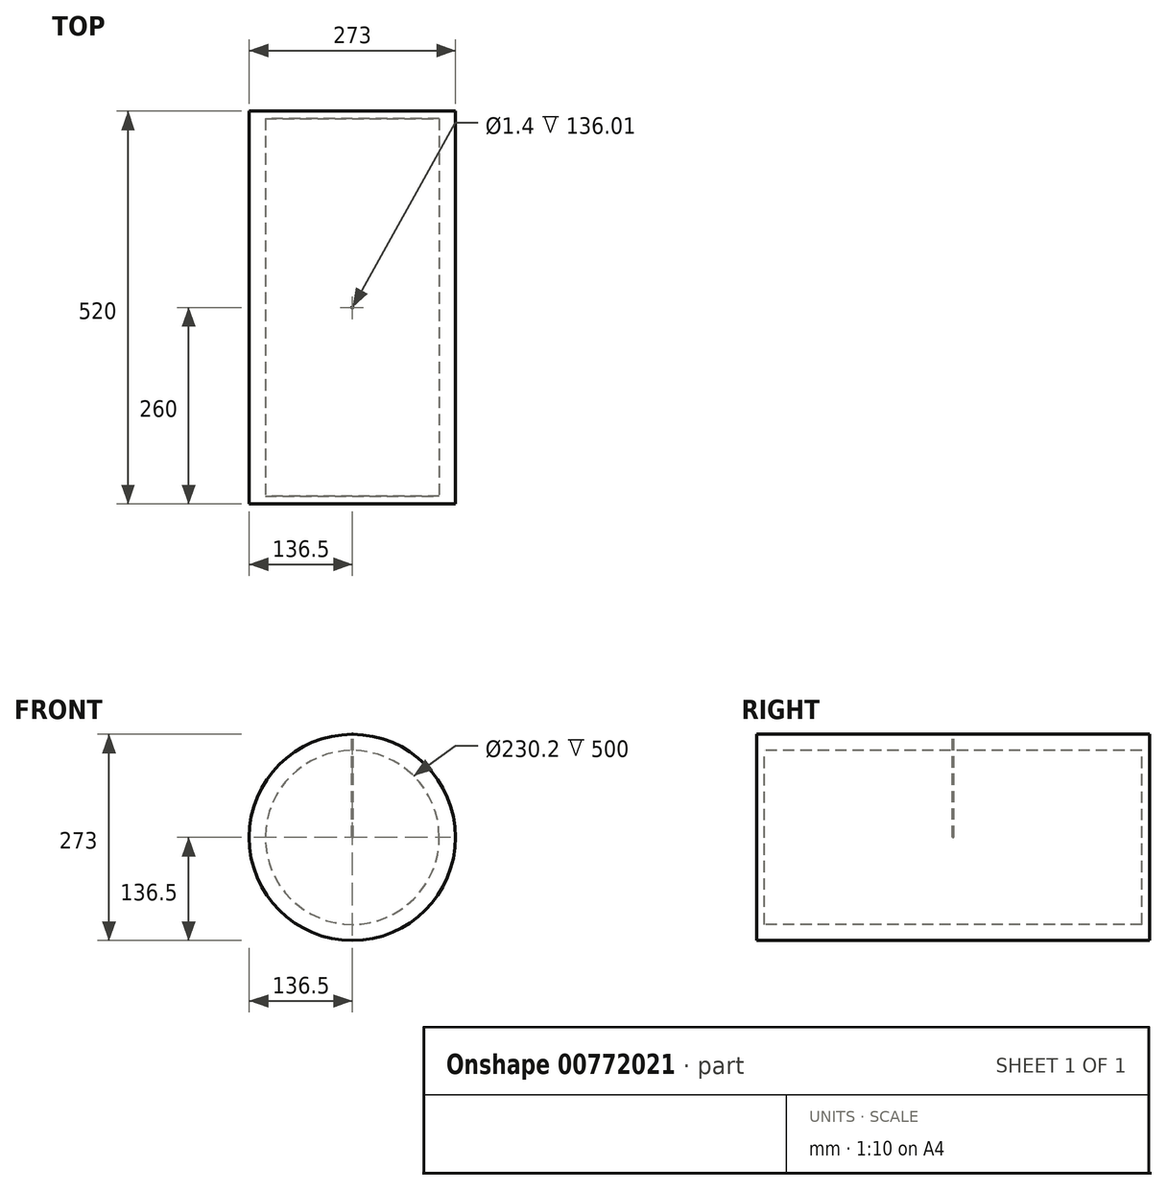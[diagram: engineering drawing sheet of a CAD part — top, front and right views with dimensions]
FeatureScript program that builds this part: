
annotation { "Feature Type Name" : "Feature", "Feature Type Description" : "" }
export const myFeature = defineFeature(function(context is Context, id is Id, definition is map)
    precondition{}
    {
        {
            var Q0;
            Q0=qCreatedBy(makeId("Right.planeOp"),FACE);
            var sketch = newSketch(context, id + "F0", { "sketchPlane" : qUnion([Q0])});
            skLineSegment(sketch, "E0", {"start": v(0, 0) * mm, "end": v(1, 0) * mm});
            skLineSegment(sketch, "E1", {"start": v(0, 0) * mm, "end": v(-1, 0) * mm});
            skLineSegment(sketch, "E2", {"start": v(-1, 0) * mm, "end": v(-1, -136) * mm});
            skLineSegment(sketch, "E3", {"start": v(1, 0) * mm, "end": v(1, -136.01) * mm});
            skArc(sketch, "E4", {"start": v(1, -136) * mm, "mid": v(0, -137) * mm, "end": v(-1, -136) * mm});
            skPoint(sketch, "E5", {"position": v(-0.7, 0) * mm});
            skPoint(sketch, "E6", {"position": v(0.7, 0) * mm});
            skLineSegment(sketch, "E7", {"start": v(-0.7, 0) * mm, "end": v(-0.7, -136) * mm});
            skLineSegment(sketch, "E8", {"start": v(0.7, 0) * mm, "end": v(0.7, -136) * mm});
            skLineSegment(sketch, "E9", {"start": v(-0.7, -136) * mm, "end": v(0.7, -136) * mm});
            skLineSegment(sketch, "E10", {"start": v(0, 763.5) * mm, "end": v(0, -236.5) * mm});
            skPoint(sketch, "E11", {"position": v(0, -21.4) * mm});
            skLineSegment(sketch, "E12", {"start": v(0, -21.4) * mm, "end": v(-250, -21.4) * mm});
            skLineSegment(sketch, "E13", {"start": v(0, 0) * mm, "end": v(-250, 0) * mm});
            skLineSegment(sketch, "E14", {"start": v(0, -21.4) * mm, "end": v(250, -21.4) * mm});
            skLineSegment(sketch, "E15", {"start": v(0, 0) * mm, "end": v(250, 0) * mm});
            skLineSegment(sketch, "E16", {"start": v(250, 0) * mm, "end": v(250, -21.4) * mm});
            skLineSegment(sketch, "E17", {"start": v(-250, 0) * mm, "end": v(-250, -21.4) * mm});
            skLineSegment(sketch, "E18", {"start": v(-250, 0) * mm, "end": v(-260, 0) * mm});
            skLineSegment(sketch, "E19", {"start": v(-260, 0) * mm, "end": v(-260, -21.4) * mm});
            skLineSegment(sketch, "E20", {"start": v(-260, -21.4) * mm, "end": v(-250, -21.4) * mm});
            skLineSegment(sketch, "E21", {"start": v(250, 0) * mm, "end": v(260, 0) * mm});
            skLineSegment(sketch, "E22", {"start": v(260, 0) * mm, "end": v(260, -21.4) * mm});
            skLineSegment(sketch, "E23", {"start": v(260, -21.4) * mm, "end": v(250, -21.4) * mm});
            skLineSegment(sketch, "E24", {"start": v(-260, -136.5) * mm, "end": v(260, -136.5) * mm});
            skLineSegment(sketch, "E25", {"start": v(-250, -21.4) * mm, "end": v(-250, -136.5) * mm});
            skLineSegment(sketch, "E26", {"start": v(-260, -21.4) * mm, "end": v(-260, -136.5) * mm});
            skLineSegment(sketch, "E27", {"start": v(260, -21.4) * mm, "end": v(260, -136.5) * mm});
            skLineSegment(sketch, "E28", {"start": v(250, -21.4) * mm, "end": v(250, -136.5) * mm});
            skSolve(sketch);
        }
        {
            var Q0;
            {var subQ5=sQuery(id+"F0.wireOp",EDGE,"E12");var subQ8=sQuery(id+"F0.wireOp",EDGE,"E2");var subQ13=makeQuery(id+"F0.imprint","INTERSECT",VERTEX,{"derivedFrom":[subQ8,subQ5]});Q0=makeQuery(id+"F0.imprint","IMPRINT",FACE,{"disambiguationData":[TD([[makeQuery(id+"F0.imprint","IMPRINT",EDGE,{"disambiguationData":[TD([[subQ13,-1.0]])],"derivedFrom":subQ8}),1.0]])]});}
            var Q1;
            {var subQ0=sQuery(id+"F0.wireOp",EDGE,"E10");var subQ1=sQuery(id+"F0.wireOp",EDGE,"E4");var subQ2=makeQuery(id+"F0.imprint","INTERSECT",VERTEX,{"derivedFrom":[subQ1,subQ0]});Q1=makeQuery(id+"F0.imprint","IMPRINT",FACE,{"disambiguationData":[TD([[makeQuery(id+"F0.imprint","IMPRINT",EDGE,{"disambiguationData":[TD([[subQ2,-1.0]])],"derivedFrom":subQ1}),-1.0]])]});}
            var Q2;
            {var subQ3=sQuery(id+"F0.wireOp",EDGE,"E7");var subQ5=sQuery(id+"F0.wireOp",EDGE,"E12");var subQ6=makeQuery(id+"F0.imprint","INTERSECT",VERTEX,{"derivedFrom":[subQ3,subQ5]});Q2=makeQuery(id+"F0.imprint","IMPRINT",FACE,{"disambiguationData":[TD([[makeQuery(id+"F0.imprint","IMPRINT",EDGE,{"disambiguationData":[TD([[subQ6,1.0]])],"derivedFrom":subQ3}),-1.0]])]});}
            var Q3;
            Q3=sQuery(id+"F0.wireOp",EDGE,"E10");
            revolve(context, id + "F1", {"surfaceOperationType" : NewSurfaceOperationType.NEW, "entities" : qUnion([Q0, Q1, Q2]), "axis" : qUnion([Q3]), "revolveType" : RevolveType.FULL});
        }
        {
            var Q0;
            {var subQ3=sQuery(id+"F0.wireOp",EDGE,"E7");var subQ5=sQuery(id+"F0.wireOp",EDGE,"E12");var subQ6=makeQuery(id+"F0.imprint","INTERSECT",VERTEX,{"derivedFrom":[subQ3,subQ5]});Q0=qUnion([makeQuery(id+"F0.imprint","IMPRINT",FACE,{"disambiguationData":[TD([[makeQuery(id+"F0.imprint","IMPRINT",EDGE,{"disambiguationData":[TD([[subQ6,-1.0]])],"derivedFrom":subQ3}),1.0]])]}),makeQuery(id+"F0.imprint","IMPRINT",FACE,{"disambiguationData":[TD([[makeQuery(id+"F0.imprint","IMPRINT",EDGE,{"disambiguationData":[TD([[subQ6,1.0]])],"derivedFrom":subQ3}),1.0]])]})]);}
            var Q1;
            Q1=sQuery(id+"F0.wireOp",EDGE,"E10");
            revolve(context, id + "F2", {"surfaceOperationType" : NewSurfaceOperationType.NEW, "entities" : qUnion([Q0]), "axis" : qUnion([Q1]), "revolveType" : RevolveType.FULL});
        }
        {
            var Q0;
            Q0=makeQuery(id+"F0.imprint","IMPRINT",FACE,{"disambiguationData":[TD([[makeQuery(id+"F0.imprint","IMPRINT",EDGE,{"derivedFrom":sQuery(id+"F0.wireOp",EDGE,"E16")}),1.0]])]});
            var Q1;
            Q1=makeQuery(id+"F0.imprint","IMPRINT",FACE,{"disambiguationData":[TD([[makeQuery(id+"F0.imprint","IMPRINT",EDGE,{"derivedFrom":sQuery(id+"F0.wireOp",EDGE,"E23")}),1.0]])]});
            var Q2;
            {var subQ0=sQuery(id+"F0.wireOp",EDGE,"E15");Q2=makeQuery(id+"F0.imprint","IMPRINT",FACE,{"disambiguationData":[TD([[makeQuery(id+"F0.imprint","IMPRINT",EDGE,{"derivedFrom":subQ0}),-1.0]])]});}
            var Q3;
            {var subQ0=sQuery(id+"F0.wireOp",EDGE,"E13");Q3=makeQuery(id+"F0.imprint","IMPRINT",FACE,{"disambiguationData":[TD([[makeQuery(id+"F0.imprint","IMPRINT",EDGE,{"derivedFrom":subQ0}),1.0]])]});}
            var Q4;
            {var subQ3=sQuery(id+"F0.wireOp",EDGE,"E8");var subQ5=sQuery(id+"F0.wireOp",EDGE,"E14");var subQ7=makeQuery(id+"F0.imprint","INTERSECT",VERTEX,{"derivedFrom":[subQ3,subQ5]});Q4=makeQuery(id+"F0.imprint","IMPRINT",FACE,{"disambiguationData":[TD([[makeQuery(id+"F0.imprint","IMPRINT",EDGE,{"disambiguationData":[TD([[subQ7,1.0]])],"derivedFrom":subQ3}),1.0]])]});}
            var Q5;
            {var subQ3=sQuery(id+"F0.wireOp",EDGE,"E7");var subQ5=sQuery(id+"F0.wireOp",EDGE,"E12");var subQ6=makeQuery(id+"F0.imprint","INTERSECT",VERTEX,{"derivedFrom":[subQ3,subQ5]});Q5=makeQuery(id+"F0.imprint","IMPRINT",FACE,{"disambiguationData":[TD([[makeQuery(id+"F0.imprint","IMPRINT",EDGE,{"disambiguationData":[TD([[subQ6,1.0]])],"derivedFrom":subQ3}),-1.0]])]});}
            var Q6;
            {var subQ3=sQuery(id+"F0.wireOp",EDGE,"E8");var subQ5=sQuery(id+"F0.wireOp",EDGE,"E14");var subQ6=makeQuery(id+"F0.imprint","INTERSECT",VERTEX,{"derivedFrom":[subQ3,subQ5]});Q6=makeQuery(id+"F0.imprint","IMPRINT",FACE,{"disambiguationData":[TD([[makeQuery(id+"F0.imprint","IMPRINT",EDGE,{"disambiguationData":[TD([[subQ6,1.0]])],"derivedFrom":subQ3}),-1.0]])]});}
            var Q7;
            {var subQ3=sQuery(id+"F0.wireOp",EDGE,"E7");var subQ5=sQuery(id+"F0.wireOp",EDGE,"E12");var subQ6=makeQuery(id+"F0.imprint","INTERSECT",VERTEX,{"derivedFrom":[subQ3,subQ5]});Q7=makeQuery(id+"F0.imprint","IMPRINT",FACE,{"disambiguationData":[TD([[makeQuery(id+"F0.imprint","IMPRINT",EDGE,{"disambiguationData":[TD([[subQ6,1.0]])],"derivedFrom":subQ3}),1.0]])]});}
            var Q8;
            Q8=makeQuery(id+"F0.imprint","IMPRINT",FACE,{"disambiguationData":[TD([[makeQuery(id+"F0.imprint","IMPRINT",EDGE,{"derivedFrom":sQuery(id+"F0.wireOp",EDGE,"E17")}),-1.0]])]});
            var Q9;
            Q9=makeQuery(id+"F0.imprint","IMPRINT",FACE,{"disambiguationData":[TD([[makeQuery(id+"F0.imprint","IMPRINT",EDGE,{"derivedFrom":sQuery(id+"F0.wireOp",EDGE,"E20")}),-1.0]])]});
            var Q10;
            Q10=sQuery(id+"F0.wireOp",EDGE,"E24");
            revolve(context, id + "F3", {"surfaceOperationType" : NewSurfaceOperationType.NEW, "entities" : qUnion([Q0, Q1, Q2, Q3, Q4, Q5, Q6, Q7, Q8, Q9]), "axis" : qUnion([Q10]), "revolveType" : RevolveType.FULL});
        }
    });
